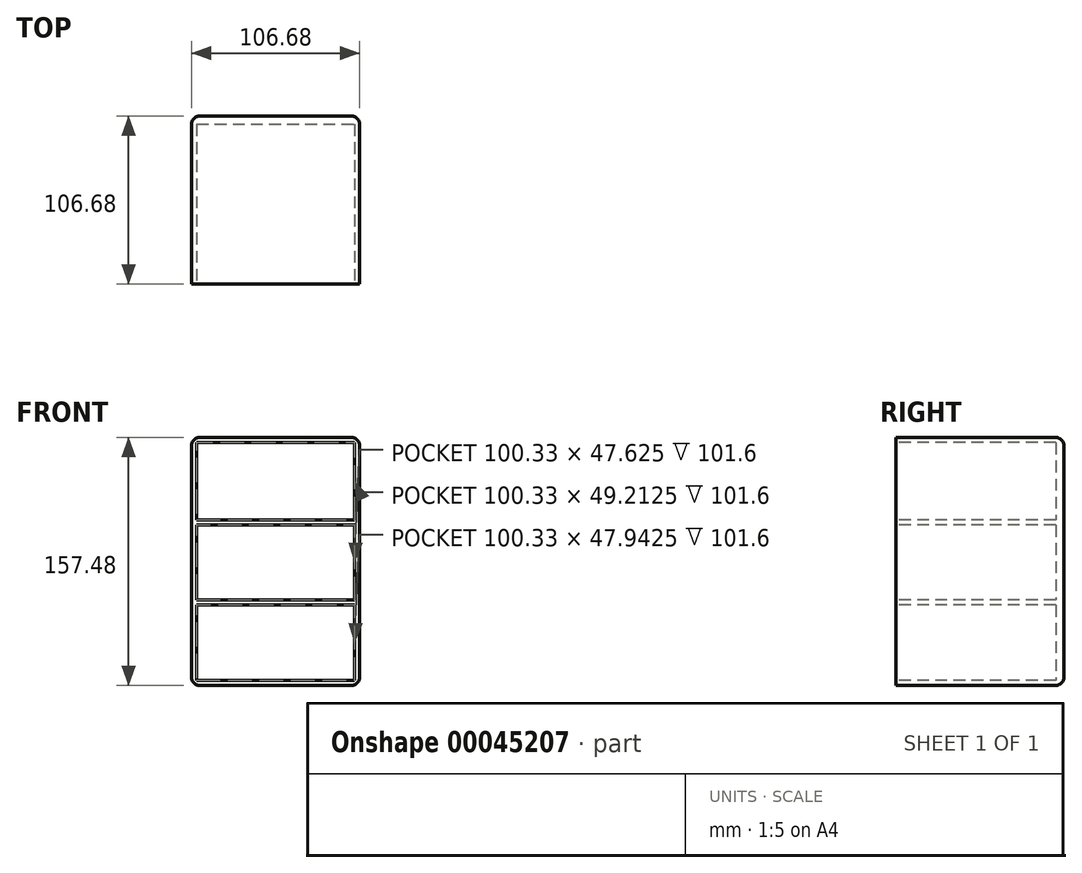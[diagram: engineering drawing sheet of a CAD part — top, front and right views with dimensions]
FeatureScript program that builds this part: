
annotation { "Feature Type Name" : "Feature", "Feature Type Description" : "" }
export const myFeature = defineFeature(function(context is Context, id is Id, definition is map)
    precondition{}
    {
        {
            var Q0;
            Q0=qCreatedBy(makeId("Front.planeOp"),FACE);
            var sketch = newSketch(context, id + "F0", { "sketchPlane" : qUnion([Q0])});
            skLineSegment(sketch, "E0.bottom", {"start": v(-51.12, 110.97) * mm, "end": v(55.56, 110.97) * mm});
            skLineSegment(sketch, "E0.top", {"start": v(-51.12, -46.51) * mm, "end": v(55.56, -46.51) * mm});
            skLineSegment(sketch, "E0.left", {"start": v(-51.12, 110.97) * mm, "end": v(-51.12, -46.51) * mm});
            skLineSegment(sketch, "E0.right", {"start": v(55.56, 110.97) * mm, "end": v(55.56, -46.51) * mm});
            skSolve(sketch);
        }
        {
            var Q0;
            Q0 = qSketchRegion(id + "F0", true);
            extrude(context, id + "F1", {"entities" : qUnion([Q0]), "depth" : 106.68 * mm});
        }
        {
            var Q0;
            Q0=makeQuery(id+"F1.opExtrude","CAP_FACE",FACE,{"disambiguationData":[OSD([sQuery(id+"F0.wireOp",EDGE,"E0.bottom"),sQuery(id+"F0.wireOp",EDGE,"E0.top"),sQuery(id+"F0.wireOp",EDGE,"E0.left"),sQuery(id+"F0.wireOp",EDGE,"E0.right")])],"isStart":false});
            var sketch = newSketch(context, id + "F2", { "sketchPlane" : qUnion([Q0])});
            skLineSegment(sketch, "E1.bottom", {"start": v(-47.94, 107.8) * mm, "end": v(52.39, 107.8) * mm});
            skLineSegment(sketch, "E1.top", {"start": v(-47.94, -43.34) * mm, "end": v(52.39, -43.34) * mm});
            skLineSegment(sketch, "E1.left", {"start": v(-47.94, 107.8) * mm, "end": v(-47.94, -43.34) * mm});
            skLineSegment(sketch, "E1.right", {"start": v(52.39, 107.8) * mm, "end": v(52.39, -43.34) * mm});
            skSolve(sketch);
        }
        {
            var Q0;
            Q0 = qSketchRegion(id + "F2", true);
            extrude(context, id + "F3", {"entities" : qUnion([Q0]), "operationType" : NewBodyOperationType.REMOVE, "oppositeDirection" : true, "depth" : 101.6 * mm});
        }
        {
            var Q0;
            Q0=makeQuery(id+"F1.opExtrude","CAP_FACE",FACE,{"disambiguationData":[OSD([sQuery(id+"F0.wireOp",EDGE,"E0.bottom"),sQuery(id+"F0.wireOp",EDGE,"E0.top"),sQuery(id+"F0.wireOp",EDGE,"E0.left"),sQuery(id+"F0.wireOp",EDGE,"E0.right")])],"isStart":false});
            var sketch = newSketch(context, id + "F4", { "sketchPlane" : qUnion([Q0])});
            skLineSegment(sketch, "E2.bottom", {"start": v(-51.12, 55.4) * mm, "end": v(55.56, 55.4) * mm});
            skLineSegment(sketch, "E2.top", {"start": v(-51.12, 58.58) * mm, "end": v(55.56, 58.58) * mm});
            skLineSegment(sketch, "E2.left", {"start": v(-51.12, 58.58) * mm, "end": v(-51.12, 55.4) * mm});
            skLineSegment(sketch, "E2.right", {"start": v(55.56, 58.58) * mm, "end": v(55.56, 55.4) * mm});
            skLineSegment(sketch, "E3.bottom", {"start": v(-51.12, 7.78) * mm, "end": v(55.56, 7.78) * mm});
            skLineSegment(sketch, "E3.top", {"start": v(-51.12, 4.6) * mm, "end": v(55.56, 4.6) * mm});
            skLineSegment(sketch, "E3.left", {"start": v(-51.12, 7.78) * mm, "end": v(-51.12, 4.6) * mm});
            skLineSegment(sketch, "E3.right", {"start": v(55.56, 7.78) * mm, "end": v(55.56, 4.6) * mm});
            skLineSegment(sketch, "E4", {"start": v(55.56, 6.2) * mm, "end": v(-51.12, 6.2) * mm});
            skLineSegment(sketch, "E5", {"start": v(-51.12, 57) * mm, "end": v(55.56, 57) * mm});
            skSolve(sketch);
        }
        {
            var Q0;
            Q0 = qSketchRegion(id + "F4", true);
            extrude(context, id + "F5", {"entities" : qUnion([Q0]), "operationType" : NewBodyOperationType.ADD, "oppositeDirection" : true, "depth" : 101.6 * mm});
        }
        {
            var Q0;
            Q0=makeQuery(id+"F1.opExtrude","SWEPT_EDGE",EDGE,{"disambiguationData":[OSD([sQuery(id+"F0.wireOp",EDGE,"E0.bottom"),sQuery(id+"F0.wireOp",EDGE,"E0.right")])]});
            var Q1;
            Q1=makeQuery(id+"F1.opExtrude","SWEPT_EDGE",EDGE,{"disambiguationData":[OSD([sQuery(id+"F0.wireOp",EDGE,"E0.bottom"),sQuery(id+"F0.wireOp",EDGE,"E0.left")])]});
            var Q2;
            Q2=makeQuery(id+"F1.opExtrude","SWEPT_EDGE",EDGE,{"disambiguationData":[OSD([sQuery(id+"F0.wireOp",EDGE,"E0.top"),sQuery(id+"F0.wireOp",EDGE,"E0.right")])]});
            var Q3;
            Q3=makeQuery(id+"F1.opExtrude","SWEPT_EDGE",EDGE,{"disambiguationData":[OSD([sQuery(id+"F0.wireOp",EDGE,"E0.top"),sQuery(id+"F0.wireOp",EDGE,"E0.left")])]});
            var Q4;
            Q4=makeQuery(id+"F1.opExtrude","CAP_EDGE",EDGE,{"disambiguationData":[OSD([sQuery(id+"F0.wireOp",EDGE,"E0.left")])],"isStart":true});
            var Q5;
            Q5=makeQuery(id+"F1.opExtrude","CAP_EDGE",EDGE,{"disambiguationData":[OSD([sQuery(id+"F0.wireOp",EDGE,"E0.bottom")])],"isStart":true});
            var Q6;
            Q6=makeQuery(id+"F1.opExtrude","CAP_EDGE",EDGE,{"disambiguationData":[OSD([sQuery(id+"F0.wireOp",EDGE,"E0.right")])],"isStart":true});
            var Q7;
            Q7=makeQuery(id+"F1.opExtrude","CAP_EDGE",EDGE,{"disambiguationData":[OSD([sQuery(id+"F0.wireOp",EDGE,"E0.top")])],"isStart":true});
            fillet(context, id + "F6", {"entities" : qUnion([Q0, Q1, Q2, Q3, Q4, Q5, Q6, Q7]), "radius" : 5.08 * mm, "tangentPropagation" : true, "allowEdgeOverflow" : false});
        }
    });
